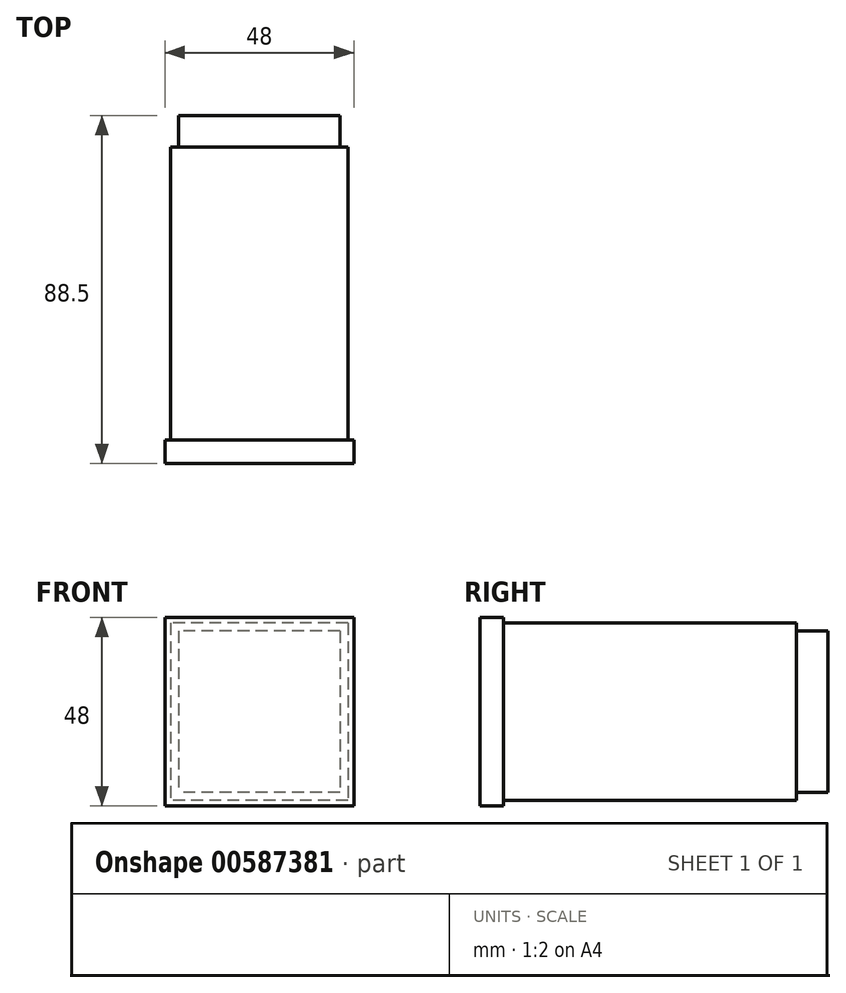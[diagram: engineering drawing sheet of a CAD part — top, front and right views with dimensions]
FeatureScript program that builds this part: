
annotation { "Feature Type Name" : "Feature", "Feature Type Description" : "" }
export const myFeature = defineFeature(function(context is Context, id is Id, definition is map)
    precondition{}
    {
        {
            var Q0;
            Q0=qCreatedBy(makeId("Front.planeOp"),FACE);
            var sketch = newSketch(context, id + "F0", { "sketchPlane" : qUnion([Q0])});
            skLineSegment(sketch, "E0.bottom", {"start": v(-24, 24) * mm, "end": v(24, 24) * mm});
            skLineSegment(sketch, "E0.top", {"start": v(-24, -24) * mm, "end": v(24, -24) * mm});
            skLineSegment(sketch, "E0.left", {"start": v(-24, 24) * mm, "end": v(-24, -24) * mm});
            skLineSegment(sketch, "E0.right", {"start": v(24, 24) * mm, "end": v(24, -24) * mm});
            skSolve(sketch);
        }
        {
            var Q0;
            Q0=makeQuery(id+"F0.imprint","IMPRINT",FACE,{"disambiguationData":[TD([[makeQuery(id+"F0.imprint","IMPRINT",EDGE,{"derivedFrom":sQuery(id+"F0.wireOp",EDGE,"E0.bottom")}),-1.0]])]});
            extrude(context, id + "F1", {"entities" : qUnion([Q0]), "depth" : 6 * mm, "offsetDistance" : 25 * mm});
        }
        {
            var Q0;
            Q0=makeQuery(id+"F1.opExtrude","CAP_FACE",FACE,{"disambiguationData":[OSD([sQuery(id+"F0.wireOp",EDGE,"E0.bottom"),sQuery(id+"F0.wireOp",EDGE,"E0.top"),sQuery(id+"F0.wireOp",EDGE,"E0.left"),sQuery(id+"F0.wireOp",EDGE,"E0.right")])],"isStart":true});
            var sketch = newSketch(context, id + "F2", { "sketchPlane" : qUnion([Q0])});
            skLineSegment(sketch, "E1.bottom", {"start": v(-22.5, 22.5) * mm, "end": v(22.5, 22.5) * mm});
            skLineSegment(sketch, "E1.top", {"start": v(-22.5, -22.5) * mm, "end": v(22.5, -22.5) * mm});
            skLineSegment(sketch, "E1.left", {"start": v(-22.5, 22.5) * mm, "end": v(-22.5, -22.5) * mm});
            skLineSegment(sketch, "E1.right", {"start": v(22.5, 22.5) * mm, "end": v(22.5, -22.5) * mm});
            skSolve(sketch);
        }
        {
            var Q0;
            Q0=makeQuery(id+"F2.imprint","IMPRINT",FACE,{"disambiguationData":[TD([[makeQuery(id+"F2.imprint","IMPRINT",EDGE,{"derivedFrom":sQuery(id+"F2.wireOp",EDGE,"E1.bottom")}),-1.0]])]});
            extrude(context, id + "F3", {"entities" : qUnion([Q0]), "operationType" : NewBodyOperationType.ADD, "depth" : 74.5 * mm, "offsetDistance" : 25 * mm});
        }
        {
            var Q0;
            Q0=makeQuery(id+"F3.opExtrude","CAP_FACE",FACE,{"disambiguationData":[OSD([sQuery(id+"F2.wireOp",EDGE,"E1.bottom"),sQuery(id+"F2.wireOp",EDGE,"E1.top"),sQuery(id+"F2.wireOp",EDGE,"E1.left"),sQuery(id+"F2.wireOp",EDGE,"E1.right")])],"isStart":false});
            var sketch = newSketch(context, id + "F4", { "sketchPlane" : qUnion([Q0])});
            skLineSegment(sketch, "E2.bottom", {"start": v(-20.5, 20.5) * mm, "end": v(20.5, 20.5) * mm});
            skLineSegment(sketch, "E2.top", {"start": v(-20.5, -20.5) * mm, "end": v(20.5, -20.5) * mm});
            skLineSegment(sketch, "E2.left", {"start": v(-20.5, 20.5) * mm, "end": v(-20.5, -20.5) * mm});
            skLineSegment(sketch, "E2.right", {"start": v(20.5, 20.5) * mm, "end": v(20.5, -20.5) * mm});
            skSolve(sketch);
        }
        {
            var Q0;
            Q0=makeQuery(id+"F4.imprint","IMPRINT",FACE,{"disambiguationData":[TD([[makeQuery(id+"F4.imprint","IMPRINT",EDGE,{"derivedFrom":sQuery(id+"F4.wireOp",EDGE,"E2.bottom")}),-1.0]])]});
            extrude(context, id + "F5", {"entities" : qUnion([Q0]), "operationType" : NewBodyOperationType.ADD, "depth" : 8 * mm, "offsetDistance" : 25 * mm});
        }
    });
